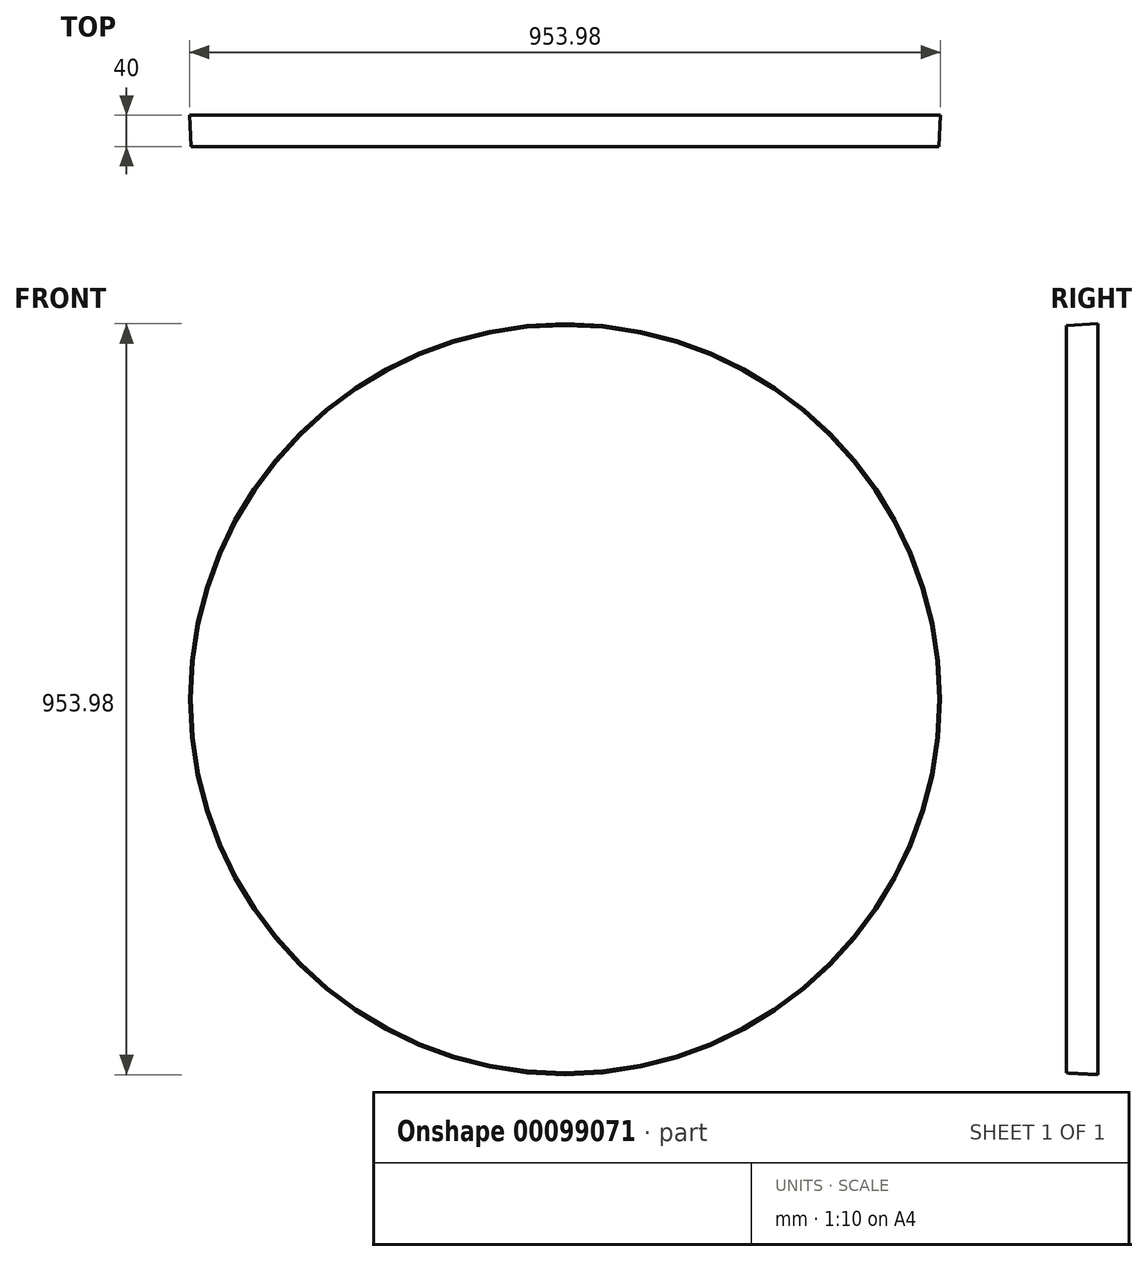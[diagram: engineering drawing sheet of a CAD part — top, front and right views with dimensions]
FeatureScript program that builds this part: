
annotation { "Feature Type Name" : "Feature", "Feature Type Description" : "" }
export const myFeature = defineFeature(function(context is Context, id is Id, definition is map)
    precondition{}
    {
        {
            var Q0;
            Q0=qCreatedBy(makeId("Front.planeOp"),FACE);
            var sketch = newSketch(context, id + "F0", { "sketchPlane" : qUnion([Q0])});
            skCircle(sketch, "E0", {"center": v(170.96, 424.78) * mm, "radius": 474.9 * mm});
            skSolve(sketch);
        }
        {
            var Q0;
            Q0=makeQuery(id+"F0.imprint","IMPRINT",FACE,{"disambiguationData":[TD([[makeQuery(id+"F0.imprint","IMPRINT",EDGE,{"derivedFrom":sQuery(id+"F0.wireOp",EDGE,"E0")}),1.0]])]});
            extrude(context, id + "F1", {"entities" : qUnion([Q0]), "oppositeDirection" : true, "depth" : 40 * mm, "hasDraft" : true, "draftAngle" : 3 * degree});
        }
    });
